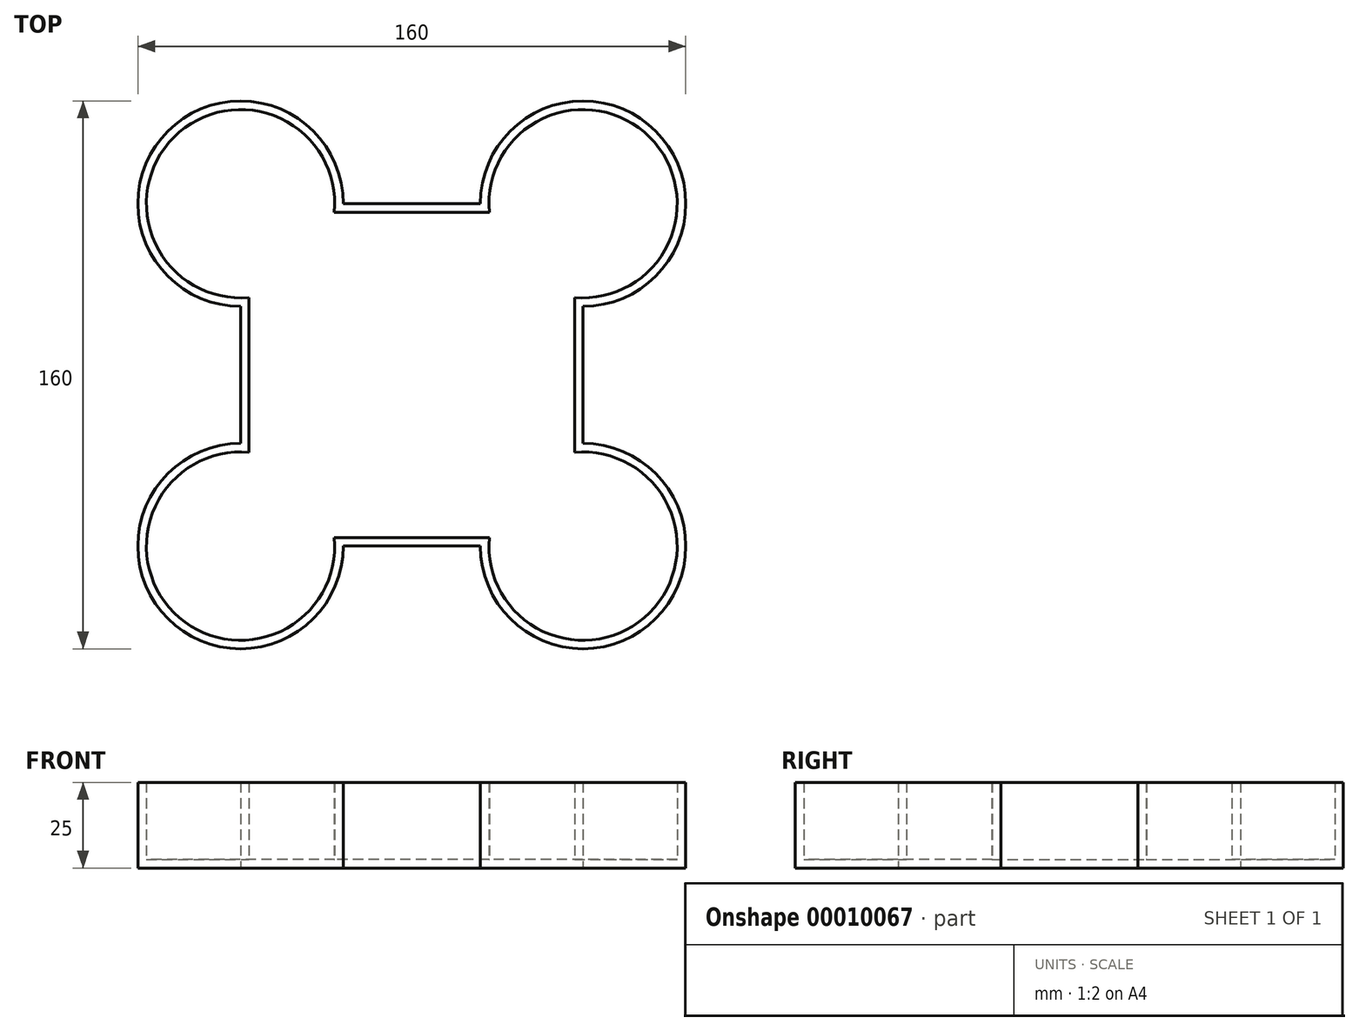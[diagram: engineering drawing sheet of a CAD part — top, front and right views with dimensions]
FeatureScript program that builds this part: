
annotation { "Feature Type Name" : "Feature", "Feature Type Description" : "" }
export const myFeature = defineFeature(function(context is Context, id is Id, definition is map)
    precondition{}
    {
        {
            var Q0;
            Q0=qCreatedBy(makeId("Top.planeOp"),FACE);
            var sketch = newSketch(context, id + "F0", { "sketchPlane" : qUnion([Q0])});
            skLineSegment(sketch, "E0.rect.bottom", {"start": v(20, -50) * mm, "end": v(-20, -50) * mm});
            skLineSegment(sketch, "E0.rect.top", {"start": v(20, 50) * mm, "end": v(-20, 50) * mm});
            skLineSegment(sketch, "E0.rect.left", {"start": v(50, -20) * mm, "end": v(50, 20) * mm});
            skLineSegment(sketch, "E0.rect.right", {"start": v(-50, -20) * mm, "end": v(-50, 20) * mm});
            skPoint(sketch, "E0.rect.middle", {"position": v(0, 0) * mm});
            skArc(sketch, "E1", {"start": v(-20, 50) * mm, "mid": v(-71.21, 71.21) * mm, "end": v(-50, 20) * mm});
            skArc(sketch, "E2", {"start": v(50, 20) * mm, "mid": v(71.21, 71.21) * mm, "end": v(20, 50) * mm});
            skArc(sketch, "E3", {"start": v(20, -50) * mm, "mid": v(71.21, -71.21) * mm, "end": v(50, -20) * mm});
            skArc(sketch, "E4", {"start": v(-50, -20) * mm, "mid": v(-71.21, -71.21) * mm, "end": v(-20, -50) * mm});
            skSolve(sketch);
        }
        {
            var Q0;
            Q0 = qSketchRegion(id + "F0", true);
            extrude(context, id + "F1", {"entities" : qUnion([Q0]), "depth" : 25 * mm});
        }
        {
            var Q0;
            Q0=makeQuery(id+"F1.opExtrude","CAP_FACE",FACE,{"disambiguationData":[OSD([sQuery(id+"F0.wireOp",EDGE,"E0.rect.bottom"),sQuery(id+"F0.wireOp",EDGE,"E0.rect.top"),sQuery(id+"F0.wireOp",EDGE,"E0.rect.left"),sQuery(id+"F0.wireOp",EDGE,"E0.rect.right"),sQuery(id+"F0.wireOp",EDGE,"E1"),sQuery(id+"F0.wireOp",EDGE,"E2"),sQuery(id+"F0.wireOp",EDGE,"E3"),sQuery(id+"F0.wireOp",EDGE,"E4")])],"isStart":false});
            shell(context, id + "F2", {"entities" : qUnion([Q0]), "thickness" : 2.5 * mm});
        }
    });
